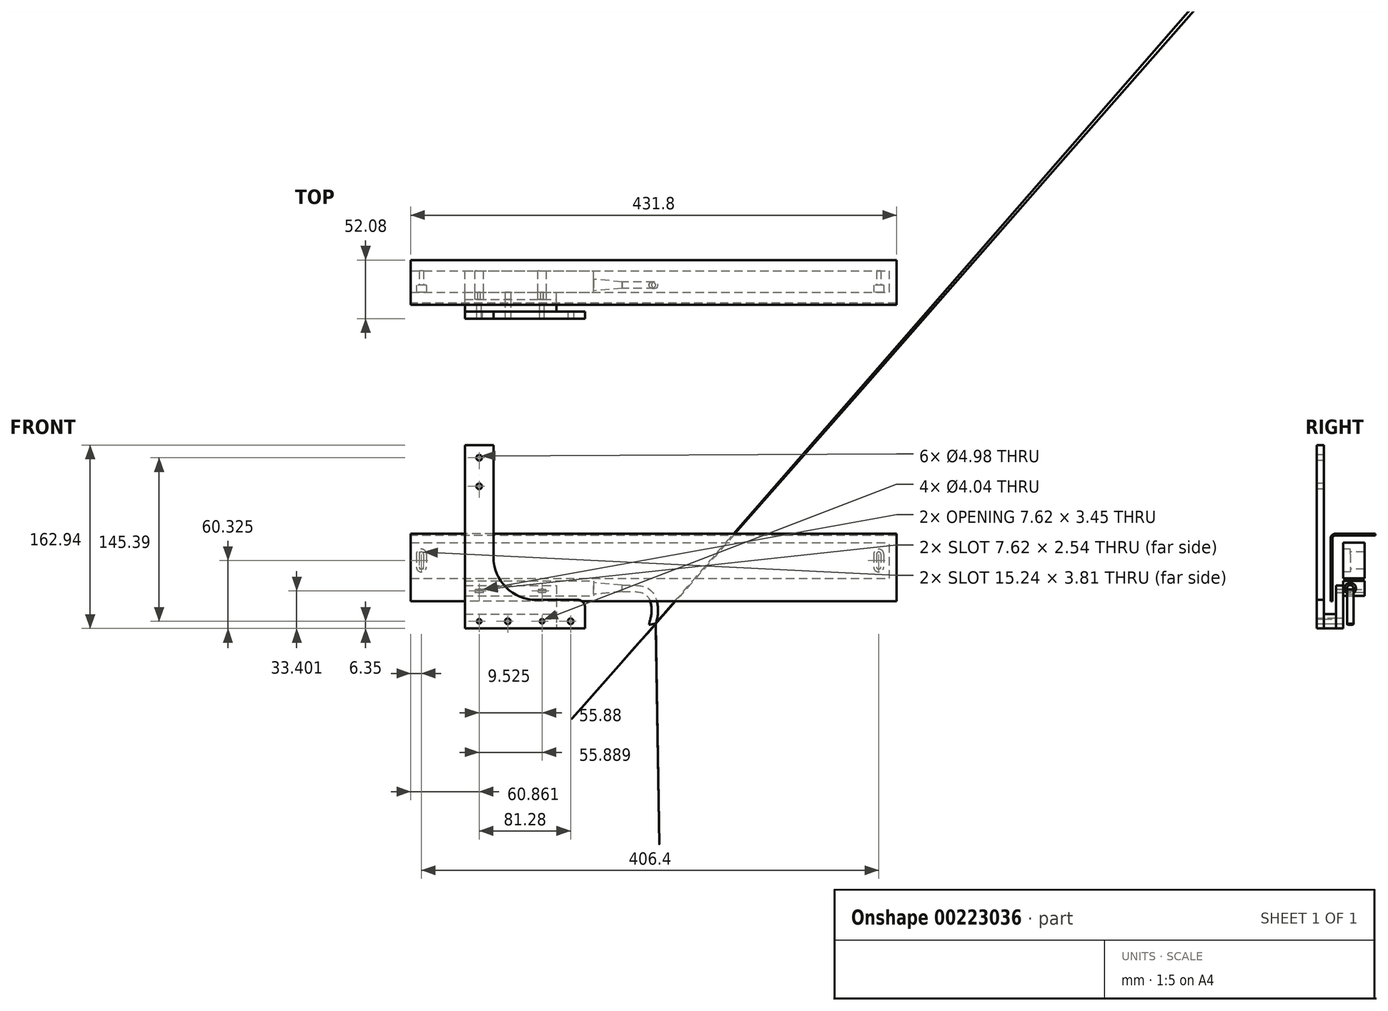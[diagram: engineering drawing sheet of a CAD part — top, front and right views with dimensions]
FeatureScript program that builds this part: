
annotation { "Feature Type Name" : "Feature", "Feature Type Description" : "" }
export const myFeature = defineFeature(function(context is Context, id is Id, definition is map)
    precondition{}
    {
        {
            var Q0;
            Q0=qCreatedBy(makeId("Front.planeOp"),FACE);
            var sketch = newSketch(context, id + "F0", { "sketchPlane" : qUnion([Q0])});
            skLineSegment(sketch, "E0.bottom", {"start": v(0, 0) * mm, "end": v(425.45, 0) * mm});
            skLineSegment(sketch, "E0.top", {"start": v(0, 31.75) * mm, "end": v(425.45, 31.75) * mm});
            skLineSegment(sketch, "E0.left", {"start": v(0, 0) * mm, "end": v(0, 31.75) * mm});
            skLineSegment(sketch, "E0.right", {"start": v(425.45, 0) * mm, "end": v(425.45, 31.75) * mm});
            skLineSegment(sketch, "E1.bottom", {"start": v(48.16, -2.29) * mm, "end": v(162.46, -2.29) * mm});
            skLineSegment(sketch, "E1.top", {"start": v(48.16, -15.62) * mm, "end": v(162.46, -15.62) * mm});
            skLineSegment(sketch, "E1.left", {"start": v(48.16, -2.29) * mm, "end": v(48.16, -15.62) * mm});
            skLineSegment(sketch, "E1.right", {"start": v(162.46, -2.29) * mm, "end": v(162.46, -15.62) * mm});
            skPoint(sketch, "E2", {"position": v(60.86, -11.05) * mm});
            skPoint(sketch, "E3", {"position": v(116.74, -11.05) * mm});
            skLineSegment(sketch, "E4", {"start": v(58.32, -11.05) * mm, "end": v(63.4, -11.05) * mm});
            skLineSegment(sketch, "E5", {"start": v(114.2, -11.1) * mm, "end": v(119.29, -11.1) * mm});
            skArc(sketch, "E6.0.startCap", {"start": v(114.2, -12.38) * mm, "mid": v(112.94, -11.1) * mm, "end": v(114.2, -9.84) * mm});
            skArc(sketch, "E6.0.endCap", {"start": v(119.29, -9.84) * mm, "mid": v(120.56, -11.1) * mm, "end": v(119.29, -12.38) * mm});
            skLineSegment(sketch, "E6.0.left", {"start": v(114.2, -9.84) * mm, "end": v(119.29, -9.84) * mm});
            skLineSegment(sketch, "E6.0.right", {"start": v(114.2, -12.38) * mm, "end": v(119.29, -12.38) * mm});
            skArc(sketch, "E7.0.startCap", {"start": v(58.32, -12.32) * mm, "mid": v(57.05, -11.05) * mm, "end": v(58.32, -9.78) * mm});
            skArc(sketch, "E7.0.endCap", {"start": v(63.4, -9.78) * mm, "mid": v(64.67, -11.05) * mm, "end": v(63.4, -12.32) * mm});
            skLineSegment(sketch, "E7.0.left", {"start": v(58.32, -9.78) * mm, "end": v(63.4, -9.78) * mm});
            skLineSegment(sketch, "E7.0.right", {"start": v(58.32, -12.32) * mm, "end": v(63.4, -12.32) * mm});
            skSolve(sketch);
        }
        {
            var Q0;
            Q0=makeQuery(id+"F0.imprint","IMPRINT",FACE,{"disambiguationData":[TD([[makeQuery(id+"F0.imprint","IMPRINT",EDGE,{"derivedFrom":sQuery(id+"F0.wireOp",EDGE,"E0.bottom")}),1.0]])]});
            extrude(context, id + "F1", {"entities" : qUnion([Q0]), "depth" : 19.05 * mm});
        }
        {
            var Q0;
            Q0=makeQuery(id+"F0.imprint","IMPRINT",FACE,{"disambiguationData":[TD([[makeQuery(id+"F0.imprint","IMPRINT",EDGE,{"derivedFrom":sQuery(id+"F0.wireOp",EDGE,"E1.bottom")}),-1.0]])]});
            extrude(context, id + "F2", {"entities" : qUnion([Q0]), "depth" : 19.05 * mm});
        }
        {
            var Q0;
            Q0=makeQuery(id+"F2.opExtrude","SWEPT_FACE",FACE,{"disambiguationData":[OSD([sQuery(id+"F0.wireOp",EDGE,"E1.right")])]});
            var sketch = newSketch(context, id + "F3", { "sketchPlane" : qUnion([Q0])});
            skCircle(sketch, "E8", {"center": v(-12.7, -8.95) * mm, "radius": 5.08 * mm});
            skSolve(sketch);
        }
        {
            var Q0;
            Q0=makeQuery(id+"F3.imprint","IMPRINT",FACE,{"disambiguationData":[TD([[makeQuery(id+"F3.imprint","IMPRINT",EDGE,{"derivedFrom":sQuery(id+"F3.wireOp",EDGE,"E8")}),1.0]])]});
            extrude(context, id + "F4", {"entities" : qUnion([Q0]), "operationType" : NewBodyOperationType.ADD, "depth" : 25.4 * mm, "hasDraft" : true, "draftAngle" : 5 * degree, "draftPullDirection" : true});
        }
        {
            var Q0;
            Q0=makeQuery(id+"F2.opExtrude","CAP_FACE",FACE,{"disambiguationData":[OSD([sQuery(id+"F0.wireOp",EDGE,"E1.bottom"),sQuery(id+"F0.wireOp",EDGE,"E1.top"),sQuery(id+"F0.wireOp",EDGE,"E1.left"),sQuery(id+"F0.wireOp",EDGE,"E1.right")])],"isStart":false});
            cPlane(context, id + "F5", {"entities" : qUnion([Q0]), "cplaneType" : CPlaneType.OFFSET, "offset" : 6.35 * mm, "oppositeDirection" : true, "width" : 152.4 * mm, "height" : 152.4 * mm});
        }
        {
            var Q0;
            Q0=qCreatedBy(id+"F5.planeOp",FACE);
            var sketch = newSketch(context, id + "F6", { "sketchPlane" : qUnion([Q0])});
            skLineSegment(sketch, "E9", {"start": v(188.18, -11.78) * mm, "end": v(162.46, -14.03) * mm});
            skLineSegment(sketch, "E10", {"start": v(162.46, -3.87) * mm, "end": v(187.86, -6.1) * mm});
            skLineSegment(sketch, "E11", {"start": v(187.86, -6.1) * mm, "end": v(188.18, -11.78) * mm, "construction": true});
            skLineSegment(sketch, "E12", {"start": v(188.02, -8.94) * mm, "end": v(188.34, -8.92) * mm});
            skFitSpline(sketch, "E13", {"points": [v(188.34, -8.92) * mm, v(199.58, -8.92) * mm, v(208.96, -11.04) * mm, v(215.92, -20.72) * mm, v(216.25, -34.87) * mm, v(214.71, -41.15) * mm], "startDerivative": vector(119.2, 4.39) * mm, "endDerivative": vector(2.07, -9.5) * mm});
            skSolve(sketch);
        }
        {
            var Q0;
            Q0=makeQuery(id+"F4.opExtrude","CAP_FACE",FACE,{"disambiguationData":[OSD([sQuery(id+"F3.wireOp",EDGE,"E8")])],"isStart":false});
            var Q1;
            Q1=sQuery(id+"F6.wireOp",EDGE,"E13");
            sweep(context, id + "F7", {"operationType" : NewBodyOperationType.ADD, "profiles" : qUnion([Q0]), "path" : qUnion([Q1])});
        }
        {
            var Q0;
            Q0=makeQuery(id+"F1.opExtrude","CAP_FACE",FACE,{"disambiguationData":[OSD([sQuery(id+"F0.wireOp",EDGE,"E0.bottom"),sQuery(id+"F0.wireOp",EDGE,"E0.top"),sQuery(id+"F0.wireOp",EDGE,"E0.left"),sQuery(id+"F0.wireOp",EDGE,"E0.right")])],"isStart":false});
            var sketch = newSketch(context, id + "F8", { "sketchPlane" : qUnion([Q0])});
            skArc(sketch, "E14", {"start": v(13.97, 21.59) * mm, "mid": v(9.53, 26.04) * mm, "end": v(5.08, 21.59) * mm});
            skArc(sketch, "E15.0.1.0", {"start": v(5.08, 10.16) * mm, "mid": v(9.53, 5.71) * mm, "end": v(13.97, 10.16) * mm});
            skArc(sketch, "E15.1.0.0", {"start": v(420.37, 21.59) * mm, "mid": v(415.93, 26.04) * mm, "end": v(411.48, 21.59) * mm});
            skArc(sketch, "E15.1.1.0", {"start": v(411.48, 10.16) * mm, "mid": v(415.93, 5.71) * mm, "end": v(420.37, 10.16) * mm});
            skLineSegment(sketch, "E15.direction1", {"start": v(9.53, 21.59) * mm, "end": v(415.93, 21.59) * mm, "construction": true});
            skLineSegment(sketch, "E15.direction2", {"start": v(9.53, 21.59) * mm, "end": v(9.53, 10.16) * mm, "construction": true});
            skLineSegment(sketch, "E16", {"start": v(5.08, 21.59) * mm, "end": v(5.08, 10.16) * mm});
            skLineSegment(sketch, "E17", {"start": v(13.97, 21.59) * mm, "end": v(13.97, 10.16) * mm});
            skLineSegment(sketch, "E18", {"start": v(411.48, 21.59) * mm, "end": v(411.48, 10.16) * mm});
            skLineSegment(sketch, "E19", {"start": v(420.37, 21.59) * mm, "end": v(420.37, 10.16) * mm});
            skArc(sketch, "E20.0", {"start": v(11.43, 21.59) * mm, "mid": v(9.53, 23.5) * mm, "end": v(7.62, 21.59) * mm});
            skLineSegment(sketch, "E20.1", {"start": v(11.43, 21.59) * mm, "end": v(11.43, 10.16) * mm});
            skArc(sketch, "E20.2", {"start": v(7.62, 10.16) * mm, "mid": v(9.53, 8.25) * mm, "end": v(11.43, 10.16) * mm});
            skLineSegment(sketch, "E20.3", {"start": v(7.62, 21.59) * mm, "end": v(7.62, 10.16) * mm});
            skArc(sketch, "E21.0", {"start": v(417.83, 21.59) * mm, "mid": v(415.93, 23.5) * mm, "end": v(414.02, 21.59) * mm});
            skLineSegment(sketch, "E21.1", {"start": v(417.83, 21.59) * mm, "end": v(417.83, 10.16) * mm});
            skArc(sketch, "E21.2", {"start": v(414.02, 10.16) * mm, "mid": v(415.93, 8.25) * mm, "end": v(417.83, 10.16) * mm});
            skLineSegment(sketch, "E21.3", {"start": v(414.02, 21.59) * mm, "end": v(414.02, 10.16) * mm});
            skSolve(sketch);
        }
        {
            var Q0;
            {var subQ0=sQuery(id+"F8.wireOp",EDGE,"E15.1.0.0");var subQ1=makeQuery(id+"F8.imprint","INTERSECT",VERTEX,{"derivedFrom":[subQ0,sQuery(id+"F8.wireOp",EDGE,"E18")]});Q0=makeQuery(id+"F8.imprint","IMPRINT",FACE,{"disambiguationData":[TD([[makeQuery(id+"F8.imprint","IMPRINT",EDGE,{"disambiguationData":[TD([[subQ1,1.0]])],"derivedFrom":subQ0}),1.0]])]});}
            var Q1;
            {var subQ0=sQuery(id+"F8.wireOp",EDGE,"E18");Q1=makeQuery(id+"F8.imprint","IMPRINT",FACE,{"disambiguationData":[TD([[makeQuery(id+"F8.imprint","IMPRINT",EDGE,{"derivedFrom":subQ0}),1.0]])]});}
            var Q2;
            {var subQ0=sQuery(id+"F8.wireOp",EDGE,"E15.1.1.0");var subQ1=makeQuery(id+"F8.imprint","INTERSECT",VERTEX,{"derivedFrom":[subQ0,sQuery(id+"F8.wireOp",EDGE,"E18")]});Q2=makeQuery(id+"F8.imprint","IMPRINT",FACE,{"disambiguationData":[TD([[makeQuery(id+"F8.imprint","IMPRINT",EDGE,{"disambiguationData":[TD([[subQ1,1.0]])],"derivedFrom":subQ0}),1.0]])]});}
            var Q3;
            {var subQ0=sQuery(id+"F8.wireOp",EDGE,"E14");var subQ1=makeQuery(id+"F8.imprint","INTERSECT",VERTEX,{"derivedFrom":[subQ0,sQuery(id+"F8.wireOp",EDGE,"E16")]});Q3=makeQuery(id+"F8.imprint","IMPRINT",FACE,{"disambiguationData":[TD([[makeQuery(id+"F8.imprint","IMPRINT",EDGE,{"disambiguationData":[TD([[subQ1,1.0]])],"derivedFrom":subQ0}),1.0]])]});}
            var Q4;
            {var subQ0=sQuery(id+"F8.wireOp",EDGE,"E15.0.1.0");var subQ1=makeQuery(id+"F8.imprint","INTERSECT",VERTEX,{"derivedFrom":[subQ0,sQuery(id+"F8.wireOp",EDGE,"E16")]});Q4=makeQuery(id+"F8.imprint","IMPRINT",FACE,{"disambiguationData":[TD([[makeQuery(id+"F8.imprint","IMPRINT",EDGE,{"disambiguationData":[TD([[subQ1,1.0]])],"derivedFrom":subQ0}),1.0]])]});}
            var Q5;
            {var subQ0=sQuery(id+"F8.wireOp",EDGE,"E16");Q5=makeQuery(id+"F8.imprint","IMPRINT",FACE,{"disambiguationData":[TD([[makeQuery(id+"F8.imprint","IMPRINT",EDGE,{"derivedFrom":subQ0}),1.0]])]});}
            extrude(context, id + "F9", {"entities" : qUnion([Q0, Q1, Q2, Q3, Q4, Q5]), "operationType" : NewBodyOperationType.REMOVE, "oppositeDirection" : true, "depth" : 6.35 * mm});
        }
        {
            var Q0;
            Q0=makeQuery(id+"F9.boolean.opBoolean","SPLIT",FACE,{"disambiguationData":[TD([makeQuery(id+"F9.opExtrude","SWEPT_FACE",FACE,{"disambiguationData":[OSD([sQuery(id+"F8.wireOp",EDGE,"E20.0")])]})])],"derivedFrom":makeQuery(id+"F1.opExtrude","CAP_FACE",FACE,{"disambiguationData":[OSD([sQuery(id+"F0.wireOp",EDGE,"E0.bottom"),sQuery(id+"F0.wireOp",EDGE,"E0.top"),sQuery(id+"F0.wireOp",EDGE,"E0.left"),sQuery(id+"F0.wireOp",EDGE,"E0.right")])],"isStart":false})});
            var Q1;
            Q1=makeQuery(id+"F9.boolean.opBoolean","SPLIT",FACE,{"disambiguationData":[TD([makeQuery(id+"F9.opExtrude","SWEPT_FACE",FACE,{"disambiguationData":[OSD([sQuery(id+"F8.wireOp",EDGE,"E21.0")])]})])],"derivedFrom":makeQuery(id+"F1.opExtrude","CAP_FACE",FACE,{"disambiguationData":[OSD([sQuery(id+"F0.wireOp",EDGE,"E0.bottom"),sQuery(id+"F0.wireOp",EDGE,"E0.top"),sQuery(id+"F0.wireOp",EDGE,"E0.left"),sQuery(id+"F0.wireOp",EDGE,"E0.right")])],"isStart":false})});
            extrude(context, id + "F10", {"entities" : qUnion([Q0, Q1]), "operationType" : NewBodyOperationType.REMOVE, "oppositeDirection" : true, "depth" : 25.4 * mm});
        }
        {
            var Q0;
            Q0=qCreatedBy(makeId("Right.planeOp"),FACE);
            var sketch = newSketch(context, id + "F11", { "sketchPlane" : qUnion([Q0])});
            skLineSegment(sketch, "E22", {"start": v(9.53, 38.1) * mm, "end": v(-26.04, 38.1) * mm});
            skLineSegment(sketch, "E23", {"start": v(-28.57, 35.56) * mm, "end": v(-28.57, -20.32) * mm});
            skLineSegment(sketch, "E24", {"start": v(-28.57, -20.32) * mm, "end": v(-30.15, -20.32) * mm});
            skLineSegment(sketch, "E25", {"start": v(-30.15, -20.32) * mm, "end": v(-30.15, 35.56) * mm});
            skLineSegment(sketch, "E26", {"start": v(-26.04, 39.67) * mm, "end": v(9.53, 39.67) * mm});
            skLineSegment(sketch, "E27", {"start": v(9.53, 39.67) * mm, "end": v(9.53, 38.1) * mm});
            skPoint(sketch, "E28.visualSharp", {"position": v(-28.57, 38.1) * mm});
            skArc(sketch, "E28.filletArc", {"start": v(-26.04, 38.1) * mm, "mid": v(-27.83, 37.36) * mm, "end": v(-28.57, 35.56) * mm});
            skPoint(sketch, "E29.visualSharp", {"position": v(-30.15, 39.67) * mm});
            skArc(sketch, "E29.filletArc", {"start": v(-26.04, 39.67) * mm, "mid": v(-28.94, 38.47) * mm, "end": v(-30.15, 35.56) * mm});
            skSolve(sketch);
        }
        {
            var Q0;
            Q0=makeQuery(id+"F11.imprint","IMPRINT",FACE,{"disambiguationData":[TD([[makeQuery(id+"F11.imprint","IMPRINT",EDGE,{"derivedFrom":sQuery(id+"F11.wireOp",EDGE,"E22")}),-1.0]])]});
            extrude(context, id + "F12", {"entities" : qUnion([Q0]), "depth" : 431.8 * mm});
        }
        {
            var Q0;
            Q0=makeQuery(id+"F2.opExtrude","CAP_FACE",FACE,{"disambiguationData":[OSD([sQuery(id+"F0.wireOp",EDGE,"E1.bottom"),sQuery(id+"F0.wireOp",EDGE,"E1.top"),sQuery(id+"F0.wireOp",EDGE,"E1.left"),sQuery(id+"F0.wireOp",EDGE,"E1.right"),sQuery(id+"F0.wireOp",EDGE,"E6.0.startCap"),sQuery(id+"F0.wireOp",EDGE,"E6.0.endCap"),sQuery(id+"F0.wireOp",EDGE,"E6.0.left"),sQuery(id+"F0.wireOp",EDGE,"E6.0.right"),sQuery(id+"F0.wireOp",EDGE,"E7.0.startCap"),sQuery(id+"F0.wireOp",EDGE,"E7.0.endCap"),sQuery(id+"F0.wireOp",EDGE,"E7.0.left"),sQuery(id+"F0.wireOp",EDGE,"E7.0.right")])],"isStart":false});
            var sketch = newSketch(context, id + "F13", { "sketchPlane" : qUnion([Q0])});
            skLineSegment(sketch, "E30.bottom", {"start": v(48.16, -6.35) * mm, "end": v(129.44, -6.35) * mm});
            skLineSegment(sketch, "E30.top", {"start": v(48.16, -44.45) * mm, "end": v(129.44, -44.45) * mm});
            skLineSegment(sketch, "E30.left", {"start": v(48.16, -6.35) * mm, "end": v(48.16, -44.45) * mm});
            skLineSegment(sketch, "E30.right", {"start": v(129.44, -6.35) * mm, "end": v(129.44, -44.45) * mm});
            skPoint(sketch, "E31.0", {"position": v(60.86, -11.05) * mm});
            skPoint(sketch, "E32.0", {"position": v(116.75, -11.1) * mm});
            skSolve(sketch);
        }
        {
            var Q0;
            {var subQ0=sQuery(id+"F13.wireOp",EDGE,"E30.top");Q0=makeQuery(id+"F13.imprint","IMPRINT",FACE,{"disambiguationData":[TD([[makeQuery(id+"F13.imprint","IMPRINT",EDGE,{"derivedFrom":subQ0}),1.0]])]});}
            var Q1;
            {var subQ0=sQuery(id+"F13.wireOp",EDGE,"E30.bottom");Q1=makeQuery(id+"F13.imprint","IMPRINT",FACE,{"disambiguationData":[TD([[makeQuery(id+"F13.imprint","IMPRINT",EDGE,{"derivedFrom":subQ0}),-1.0]])]});}
            var Q2;
            Q2=makeQuery(id+"F13.imprint","IMPRINT",FACE,{"disambiguationData":[TD([[makeQuery(id+"F13.imprint","IMPRINT",EDGE,{"derivedFrom":makeQuery(id+"F2.opExtrude","CAP_EDGE",EDGE,{"disambiguationData":[OSD([sQuery(id+"F0.wireOp",EDGE,"E7.0.startCap")])],"isStart":false})}),-1.0]])]});
            var Q3;
            Q3=makeQuery(id+"F13.imprint","IMPRINT",FACE,{"disambiguationData":[TD([[makeQuery(id+"F13.imprint","IMPRINT",EDGE,{"derivedFrom":makeQuery(id+"F2.opExtrude","CAP_EDGE",EDGE,{"disambiguationData":[OSD([sQuery(id+"F0.wireOp",EDGE,"E6.0.startCap")])],"isStart":false})}),-1.0]])]});
            extrude(context, id + "F14", {"entities" : qUnion([Q0, Q1, Q2, Q3]), "depth" : 6.35 * mm});
        }
        {
            var Q0;
            Q0=sQuery(id+"F0.wireOp",VERTEX,"E2");
            var Q1;
            Q1=sQuery(id+"F0.wireOp",VERTEX,"E3");
            var Q2;
            Q2=makeQuery(id+"F14.opExtrude","SWEPT_BODY",BODY,{"disambiguationData":[OSD([sQuery(id+"F13.wireOp",EDGE,"E30.bottom"),sQuery(id+"F13.wireOp",EDGE,"E30.top"),sQuery(id+"F13.wireOp",EDGE,"E30.left"),sQuery(id+"F13.wireOp",EDGE,"E30.right")])]});
            hole(context, id + "F15", {"style" : HoleStyle.SIMPLE, "endStyle" : HoleEndStyle.THROUGH, "oppositeDirection" : true, "standardTappedOrClearance" : lookupTablePath({ "standard" : "ANSI", "engagement" : "75%", "pitch" : "32 tpi", "size" : "#8", "type" : "Tapped" }), "standardBlindInLast" : lookupTablePath({ "standard" : "ANSI", "engagement" : "75%", "pitch" : "32 tpi", "size" : "#8", "type" : "Tapped" }), "holeDiameter" : 3.45 * mm, "locations" : qUnion([Q0, Q1]), "scope" : qUnion([Q2]), "isTappedThrough" : true, "majorDiameter" : 4.17 * mm, "showTappedDepth" : true});
        }
        {
            var Q0;
            Q0=makeQuery(id+"F14.opExtrude","CAP_FACE",FACE,{"disambiguationData":[OSD([sQuery(id+"F13.wireOp",EDGE,"E30.bottom"),sQuery(id+"F13.wireOp",EDGE,"E30.top"),sQuery(id+"F13.wireOp",EDGE,"E30.left"),sQuery(id+"F13.wireOp",EDGE,"E30.right")])],"isStart":false});
            var sketch = newSketch(context, id + "F16", { "sketchPlane" : qUnion([Q0])});
            skLineSegment(sketch, "E33.bottom", {"start": v(48.16, -44.45) * mm, "end": v(129.44, -44.45) * mm});
            skLineSegment(sketch, "E33.top", {"start": v(48.16, -31.75) * mm, "end": v(129.44, -31.75) * mm});
            skLineSegment(sketch, "E33.left", {"start": v(48.16, -44.45) * mm, "end": v(48.16, -31.75) * mm});
            skLineSegment(sketch, "E33.right", {"start": v(129.44, -44.45) * mm, "end": v(129.44, -31.75) * mm});
            skPoint(sketch, "E34", {"position": v(60.86, -38.1) * mm});
            skPoint(sketch, "E34.positionSnap0", {"position": v(48.16, -38.1) * mm});
            skPoint(sketch, "E35", {"position": v(116.74, -38.1) * mm});
            skPoint(sketch, "E35.positionSnap0", {"position": v(129.44, -38.1) * mm});
            skSolve(sketch);
        }
        {
            var Q0;
            Q0=makeQuery(id+"F16.imprint","IMPRINT",FACE,{"disambiguationData":[TD([[makeQuery(id+"F16.imprint","IMPRINT",EDGE,{"derivedFrom":sQuery(id+"F16.wireOp",EDGE,"E33.bottom")}),1.0]])]});
            extrude(context, id + "F17", {"entities" : qUnion([Q0]), "depth" : 10.8 * mm});
        }
        {
            var Q0;
            Q0=sQuery(id+"F16.wireOp",VERTEX,"E34");
            var Q1;
            Q1=sQuery(id+"F16.wireOp",VERTEX,"E35");
            var Q2;
            Q2=makeQuery(id+"F17.opExtrude","SWEPT_BODY",BODY,{"disambiguationData":[OSD([sQuery(id+"F16.wireOp",EDGE,"E33.bottom"),sQuery(id+"F16.wireOp",EDGE,"E33.top"),sQuery(id+"F16.wireOp",EDGE,"E33.left"),sQuery(id+"F16.wireOp",EDGE,"E33.right")])]});
            hole(context, id + "F18", {"style" : HoleStyle.SIMPLE, "endStyle" : HoleEndStyle.THROUGH, "oppositeDirection" : true, "standardTappedOrClearance" : lookupTablePath({ "standard" : "ANSI", "engagement" : "75%", "pitch" : "32 tpi", "size" : "#10", "type" : "Tapped" }), "standardBlindInLast" : lookupTablePath({ "standard" : "ANSI", "engagement" : "75%", "pitch" : "32 tpi", "size" : "#10", "type" : "Tapped" }), "holeDiameter" : 4.04 * mm, "locations" : qUnion([Q0, Q1]), "scope" : qUnion([Q2]), "isTappedThrough" : true, "majorDiameter" : 4.83 * mm, "showTappedDepth" : true});
        }
        {
            var Q0;
            Q0=makeQuery(id+"F17.opExtrude","CAP_FACE",FACE,{"disambiguationData":[OSD([sQuery(id+"F16.wireOp",EDGE,"E33.bottom"),sQuery(id+"F16.wireOp",EDGE,"E33.top"),sQuery(id+"F16.wireOp",EDGE,"E33.left"),sQuery(id+"F16.wireOp",EDGE,"E33.right")])],"isStart":false});
            var sketch = newSketch(context, id + "F19", { "sketchPlane" : qUnion([Q0])});
            skPoint(sketch, "E36.0", {"position": v(48.16, -44.45) * mm});
            skLineSegment(sketch, "E37.bottom", {"start": v(48.16, -44.45) * mm, "end": v(154.84, -44.45) * mm});
            skLineSegment(sketch, "E37.top", {"start": v(48.16, 118.5) * mm, "end": v(73.56, 118.5) * mm});
            skLineSegment(sketch, "E37.left", {"start": v(48.16, -44.45) * mm, "end": v(48.16, 118.5) * mm});
            skLineSegment(sketch, "E37.right", {"start": v(154.84, -44.45) * mm, "end": v(154.84, -25.4) * mm});
            skLineSegment(sketch, "E38", {"start": v(73.56, 118.5) * mm, "end": v(73.56, 19.05) * mm});
            skLineSegment(sketch, "E39", {"start": v(111.66, -19.05) * mm, "end": v(148.5, -19.05) * mm});
            skPoint(sketch, "E40.orphan", {"position": v(129.44, 118.5) * mm});
            skPoint(sketch, "E41.visualSharp", {"position": v(73.56, -19.05) * mm});
            skArc(sketch, "E41.filletArc", {"start": v(73.56, 19.05) * mm, "mid": v(84.72, -7.9) * mm, "end": v(111.66, -19.05) * mm});
            skPoint(sketch, "E42.visualSharp", {"position": v(154.84, -19.05) * mm});
            skArc(sketch, "E42.filletArc", {"start": v(154.84, -25.4) * mm, "mid": v(152.98, -20.9) * mm, "end": v(148.5, -19.05) * mm});
            skSolve(sketch);
        }
        {
            var Q0;
            {var subQ0=sQuery(id+"F19.wireOp",EDGE,"E37.top");Q0=makeQuery(id+"F19.imprint","IMPRINT",FACE,{"disambiguationData":[TD([[makeQuery(id+"F19.imprint","IMPRINT",EDGE,{"derivedFrom":subQ0}),-1.0]])]});}
            var Q1;
            Q1=makeQuery(id+"F19.imprint","IMPRINT",FACE,{"disambiguationData":[TD([[makeQuery(id+"F19.imprint","IMPRINT",EDGE,{"derivedFrom":makeQuery(id+"F18.hole-0.boolean.opBoolean","INTERSECT",EDGE,{"derivedFrom":[makeQuery(id+"F17.opExtrude","CAP_FACE",FACE,{"disambiguationData":[OSD([sQuery(id+"F16.wireOp",EDGE,"E33.bottom"),sQuery(id+"F16.wireOp",EDGE,"E33.top"),sQuery(id+"F16.wireOp",EDGE,"E33.left"),sQuery(id+"F16.wireOp",EDGE,"E33.right")])],"isStart":false}),makeQuery(id+"F18.hole-0.opRevolve","SWEPT_FACE",FACE,{"disambiguationData":[OSD([sQuery(id+"F18.hole-0.sketch.wireOp",EDGE,"core_line_2")])]})]})}),-1.0]])]});
            var Q2;
            {var subQ2=sQuery(id+"F16.wireOp",EDGE,"E33.top");var subQ3=makeQuery(id+"F17.opExtrude","CAP_EDGE",EDGE,{"disambiguationData":[OSD([subQ2])],"isStart":false});Q2=makeQuery(id+"F19.imprint","IMPRINT",FACE,{"disambiguationData":[TD([[makeQuery(id+"F19.imprint","IMPRINT",EDGE,{"derivedFrom":subQ3}),-1.0]])]});}
            var Q3;
            Q3=makeQuery(id+"F19.imprint","IMPRINT",FACE,{"disambiguationData":[TD([[makeQuery(id+"F19.imprint","IMPRINT",EDGE,{"derivedFrom":makeQuery(id+"F18.hole-1.boolean.opBoolean","INTERSECT",EDGE,{"derivedFrom":[makeQuery(id+"F17.opExtrude","CAP_FACE",FACE,{"disambiguationData":[OSD([sQuery(id+"F16.wireOp",EDGE,"E33.bottom"),sQuery(id+"F16.wireOp",EDGE,"E33.top"),sQuery(id+"F16.wireOp",EDGE,"E33.left"),sQuery(id+"F16.wireOp",EDGE,"E33.right")])],"isStart":false}),makeQuery(id+"F18.hole-1.opRevolve","SWEPT_FACE",FACE,{"disambiguationData":[OSD([sQuery(id+"F18.hole-1.sketch.wireOp",EDGE,"core_line_2")])]})]})}),-1.0]])]});
            extrude(context, id + "F20", {"entities" : qUnion([Q0, Q1, Q2, Q3]), "depth" : 6.35 * mm});
        }
        {
            var Q0;
            Q0=makeQuery(id+"F20.opExtrude","CAP_FACE",FACE,{"disambiguationData":[OSD([sQuery(id+"F16.wireOp",EDGE,"E33.bottom"),sQuery(id+"F16.wireOp",EDGE,"E33.top"),sQuery(id+"F16.wireOp",EDGE,"E33.left"),sQuery(id+"F16.wireOp",EDGE,"E33.right"),sQuery(id+"F18.hole-0.sketch.wireOp",EDGE,"core_line_2"),sQuery(id+"F18.hole-1.sketch.wireOp",EDGE,"core_line_2"),sQuery(id+"F19.wireOp",EDGE,"E37.bottom"),sQuery(id+"F19.wireOp",EDGE,"E37.top"),sQuery(id+"F19.wireOp",EDGE,"E37.left"),sQuery(id+"F19.wireOp",EDGE,"E37.right"),sQuery(id+"F19.wireOp",EDGE,"E38"),sQuery(id+"F19.wireOp",EDGE,"E39"),sQuery(id+"F19.wireOp",EDGE,"E41.filletArc"),sQuery(id+"F19.wireOp",EDGE,"E42.filletArc")])],"isStart":false});
            var sketch = newSketch(context, id + "F21", { "sketchPlane" : qUnion([Q0])});
            skPoint(sketch, "E43", {"position": v(60.86, 81.89) * mm});
            skPoint(sketch, "E43.positionSnap0", {"position": v(60.86, 118.5) * mm});
            skPoint(sketch, "E44", {"position": v(60.86, 107.29) * mm});
            skPoint(sketch, "E45.0", {"position": v(116.74, -38.1) * mm});
            skPoint(sketch, "E46", {"position": v(142.14, -38.1) * mm});
            skPoint(sketch, "E47", {"position": v(86.26, -38.1) * mm});
            skSolve(sketch);
        }
        {
            var Q0;
            Q0=sQuery(id+"F21.wireOp",VERTEX,"E44");
            var Q1;
            Q1=sQuery(id+"F21.wireOp",VERTEX,"E43");
            var Q2;
            Q2=makeQuery(id+"F20.opExtrude","SWEPT_BODY",BODY,{"disambiguationData":[OSD([sQuery(id+"F16.wireOp",EDGE,"E33.bottom"),sQuery(id+"F16.wireOp",EDGE,"E33.top"),sQuery(id+"F16.wireOp",EDGE,"E33.left"),sQuery(id+"F16.wireOp",EDGE,"E33.right"),sQuery(id+"F18.hole-0.sketch.wireOp",EDGE,"core_line_2"),sQuery(id+"F18.hole-1.sketch.wireOp",EDGE,"core_line_2"),sQuery(id+"F19.wireOp",EDGE,"E37.bottom"),sQuery(id+"F19.wireOp",EDGE,"E37.top"),sQuery(id+"F19.wireOp",EDGE,"E37.left"),sQuery(id+"F19.wireOp",EDGE,"E37.right"),sQuery(id+"F19.wireOp",EDGE,"E38"),sQuery(id+"F19.wireOp",EDGE,"E39"),sQuery(id+"F19.wireOp",EDGE,"E41.filletArc"),sQuery(id+"F19.wireOp",EDGE,"E42.filletArc")])]});
            hole(context, id + "F22", {"style" : HoleStyle.SIMPLE, "endStyle" : HoleEndStyle.THROUGH, "standardTappedOrClearance" : lookupTablePath({ "standard" : "ANSI", "fit" : "Close", "size" : "#10", "type" : "Clearance" }), "standardBlindInLast" : lookupTablePath({ "fit" : "Close", "standard" : "ANSI", "size" : "#10", "type" : "Clearance" }), "holeDiameter" : 4.98 * mm, "locations" : qUnion([Q0, Q1]), "scope" : qUnion([Q2]), "isTappedThrough" : true});
        }
        {
            var Q0;
            Q0=sQuery(id+"F21.wireOp",VERTEX,"E46");
            var Q1;
            Q1=sQuery(id+"F21.wireOp",VERTEX,"E47");
            var Q2;
            Q2=makeQuery(id+"F14.opExtrude","SWEPT_BODY",BODY,{"disambiguationData":[OSD([sQuery(id+"F13.wireOp",EDGE,"E30.bottom"),sQuery(id+"F13.wireOp",EDGE,"E30.top"),sQuery(id+"F13.wireOp",EDGE,"E30.left"),sQuery(id+"F13.wireOp",EDGE,"E30.right")])]});
            var Q3;
            Q3=makeQuery(id+"F17.opExtrude","SWEPT_BODY",BODY,{"disambiguationData":[OSD([sQuery(id+"F16.wireOp",EDGE,"E33.bottom"),sQuery(id+"F16.wireOp",EDGE,"E33.top"),sQuery(id+"F16.wireOp",EDGE,"E33.left"),sQuery(id+"F16.wireOp",EDGE,"E33.right")])]});
            var Q4;
            Q4=makeQuery(id+"F20.opExtrude","SWEPT_BODY",BODY,{"disambiguationData":[OSD([sQuery(id+"F19.wireOp",EDGE,"E37.bottom"),sQuery(id+"F19.wireOp",EDGE,"E37.top"),sQuery(id+"F19.wireOp",EDGE,"E37.left"),sQuery(id+"F19.wireOp",EDGE,"E37.right"),sQuery(id+"F19.wireOp",EDGE,"E38"),sQuery(id+"F19.wireOp",EDGE,"E39"),sQuery(id+"F19.wireOp",EDGE,"E41.filletArc"),sQuery(id+"F19.wireOp",EDGE,"E42.filletArc")])]});
            hole(context, id + "F23", {"style" : HoleStyle.SIMPLE, "endStyle" : HoleEndStyle.THROUGH, "standardTappedOrClearance" : lookupTablePath({ "standard" : "ANSI", "fit" : "Close", "size" : "#10", "type" : "Clearance" }), "standardBlindInLast" : lookupTablePath({ "fit" : "Close", "standard" : "ANSI", "size" : "#10", "type" : "Clearance" }), "holeDiameter" : 4.98 * mm, "locations" : qUnion([Q0, Q1]), "scope" : qUnion([Q2, Q3, Q4]), "isTappedThrough" : true});
        }
    });
